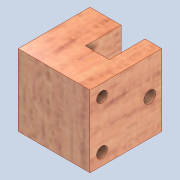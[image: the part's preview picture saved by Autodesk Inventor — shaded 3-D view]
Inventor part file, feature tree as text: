
AUTODESK INVENTOR PART (.ipt)
format: ipt  version: 2020 (Build 240168000, 168)  size: 194,048 bytes
history: native  units: mm
features: sketch x5, extrude x3, hole x2
ambient origin geometry x8: Origin, YZ Plane, XZ Plane, XY Plane, X Axis, Y Axis, Z Axis, Center Point
bodies: Solid1 (feature_tree)
feature tree (10):
  extrude  "Extrusion1"  Depth=30.0mm
  extrude  "Extrusion4"  Depth=10.0mm
  extrude  "Extrusion3"  Depth=15.0mm
  hole  "Hole1"  [1 undecoded]
  hole  "Hole2"  [1 undecoded]
  sketch  "Sketch1"  dims[d0=30.0mm d1=30.0mm]
  sketch  "Sketch4"  dims[d2=30.0mm d3=0.0mm d8=10.0mm]
  sketch  "Sketch5"  dims[d9=15.0mm d10=0.0mm d11=5.0mm]
  sketch  "Sketch6"  dims[d12=5.0mm d13=6.0mm d14=4.0mm d15=2.0mm d16=90.0deg d17=10.0mm d18=20.594885mm d19=4.5mm]
  sketch  "Sketch7"  dims[d20=5.0mm d21=5.0mm d22=5.0mm d23=0.0mm d24=0.0mm d25=7.0mm d26=4.134mm d27=10.0mm d28=4.0mm d29=2.0mm d30=90.0deg d31=10.0mm d32=20.594885mm]
note: 2 required parameter values undecoded (feature->parameter linkage not recoverable at this tier; creation-order binding heuristic only, values carry confidence <= 0.55)
